# Revit family: Legrand-Enveloppes_industrielles-Metal-Armoires_Altis-P500
name_source: partatom
category: Equipement électrique
units: mm (PartAtom-declared; Revit-internal decimal feet)

## family parameters
Basée sur le plan de construction = Non
Configuration du panneau = Deux colonnes, circuits au sein
Cote de connecteur circulaire = Utiliser le diamètre
Couper avec des vides une fois chargée = Non
Numéro OmniClass = 23.80.30.11.17
Partagée = Non
Point de calcul de pièce = Non
Titre OmniClass = Distribution Boards and Control Panels
Toujours verticalement = Oui
Type d'élément = Tableau de raccordement

## types (15) — shared parameters
Conditions Générale d'Utilisation = https://export.legrand.com
ETIM Class 6.0 = EC000261
Fabricant = Legrand
IK = 10
IP = 55
Matière = Polyester
RAL = 7035
URL = www.legrand.fr
aucun socle = Oui
erreur double hauteur de socle = Non
profondeur = 500 mm  [stored 1.64042 ft]
socle 100mm = Non
socle 200mm = Non
socle hauteur 100 largeur 1000 = Non
socle hauteur 100 largeur 1200 = Non
socle hauteur 100 largeur 1600 = Non
socle hauteur 100 largeur 400 = Non
socle hauteur 100 largeur 600 = Non
socle hauteur 100 largeur 800 = Non
socle hauteur 200 largeur 1000 = Non
socle hauteur 200 largeur 1200 = Non
socle hauteur 200 largeur 1600 = Non
socle hauteur 200 largeur 400 = Non
socle hauteur 200 largeur 600 = Non
socle hauteur 200 largeur 800 = Non
zero-valued in all types: Elévation par défaut, hauteur socles

## per-type parameters (varying)
| type | Armoire 047220 | Armoire 047221 | Armoire 047222 | Armoire 047223 | Armoire 047224 | Armoire 047225 | Armoire 047226 | Armoire 047227 | Armoire 047228 | Armoire 047229 | Armoire 047230 | Armoire 047231 | Armoire 047232 | Armoire 047233 | Armoire 047234 | Description | Hauteur | Image du type | Largeur | Poids | distance avant zone d'installation | largeur zone d'installation | profondeur zone d'installation |
| Enveloppe industrielle - Altis - Assemblable - Métal - Profondeur 500mm - Hauteur 1600mm - Largeur  600mm | Oui | Non | Non | Non | Non | Non | Non | Non | Non | Non | Non | Non | Non | Non | Non | Ref 047220 - Enveloppe industrielle - Altis - Assemblable - Métal - Profondeur 500mm | 1623 mm  [stored 5.3248 ft] | Altis_047101_pw_133028_pz_48.jpg | 600 mm | 70.40 kg | 600 mm | 2200 mm | 1100 mm |
| Enveloppe industrielle - Altis - Assemblable - Métal - Profondeur 500mm - Hauteur 1600mm - Largeur  800mm | Non | Oui | Non | Non | Non | Non | Non | Non | Non | Non | Non | Non | Non | Non | Non | Ref 047221 - Enveloppe industrielle - Altis - Assemblable - Métal - Profondeur 500mm | 1623 mm  [stored 5.3248 ft] | Altis_047101_pw_133028_pz_48.jpg | 800 mm  [stored 2.62467 ft] | 81.00 kg | 800 mm  [stored 2.62467 ft] | 2400 mm | 1300 mm  [stored 4.26509 ft] |
| Enveloppe industrielle - Altis - Assemblable - Métal - Profondeur 500mm - Hauteur 1600mm - Largeur  1200mm | Non | Non | Oui | Non | Non | Non | Non | Non | Non | Non | Non | Non | Non | Non | Non | Ref 047222 - Enveloppe industrielle - Altis - Assemblable - Métal - Profondeur 500mm | 1623 mm  [stored 5.3248 ft] | Altis_047101_pw_133028_pz_48.jpg | 0 mm  [stored 0 ft] | 124.50 kg | 0 mm  [stored 0 ft] | 1600 mm  [stored 5.24934 ft] | 500 mm  [stored 1.64042 ft] |
| Enveloppe industrielle - Altis - Assemblable - Métal - Profondeur 500mm - Hauteur 1800mm - Largeur 400mm | Non | Non | Non | Oui | Non | Non | Non | Non | Non | Non | Non | Non | Non | Non | Non | Ref 047223 - Enveloppe industrielle - Altis - Assemblable - Métal - Profondeur 500mm | 1823 mm  [stored 5.98097 ft] | Altis_047101_pw_133028_pz_48.jpg | 400 mm  [stored 1.31234 ft] | 55.00 kg | 400 mm  [stored 1.31234 ft] | 2000 mm  [stored 6.56168 ft] | 900 mm  [stored 2.95276 ft] |
| Enveloppe industrielle - Altis - Assemblable - Métal - Profondeur 500mm - Hauteur 1800mm - Largeur 600mm | Non | Non | Non | Non | Oui | Non | Non | Non | Non | Non | Non | Non | Non | Non | Non | Ref 047224 - Enveloppe industrielle - Altis - Assemblable - Métal - Profondeur 500mm | 1823 mm  [stored 5.98097 ft] | Altis_047101_pw_133028_pz_48.jpg | 600 mm | 74.30 kg | 600 mm | 2200 mm | 1100 mm |
| Enveloppe industrielle - Altis - Assemblable - Métal - Profondeur 500mm - Hauteur 1800mm - Largeur 800mm | Non | Non | Non | Non | Non | Oui | Non | Non | Non | Non | Non | Non | Non | Non | Non | Ref 047225 - Enveloppe industrielle - Altis - Assemblable - Métal - Profondeur 500mm | 1823 mm  [stored 5.98097 ft] | Altis_047101_pw_133028_pz_48.jpg | 800 mm  [stored 2.62467 ft] | 86.00 kg | 800 mm  [stored 2.62467 ft] | 2400 mm | 1300 mm  [stored 4.26509 ft] |
| Enveloppe industrielle - Altis - Assemblable - Métal - Profondeur 500mm - Hauteur 1800mm - Largeur 1000mm - Avec recentrage porte | Non | Non | Non | Non | Non | Non | Oui | Non | Non | Non | Non | Non | Non | Non | Non | Ref 047226 - Enveloppe industrielle - Altis - Assemblable - Métal - Profondeur 500mm | 1823 mm  [stored 5.98097 ft] | <Aucun> | 1000 mm  [stored 3.28084 ft] | 99.30 kg | 1000 mm  [stored 3.28084 ft] | 2600 mm  [stored 8.53018 ft] | 1500 mm  [stored 4.92126 ft] |
| Enveloppe industrielle - Altis - Assemblable - Métal - Profondeur 500mm - Hauteur 1800mm - Largeur 1200mm | Non | Non | Non | Non | Non | Non | Non | Oui | Non | Non | Non | Non | Non | Non | Non | Ref 047227 - Enveloppe industrielle - Altis - Assemblable - Métal - Profondeur 500mm | 1823 mm  [stored 5.98097 ft] | Altis_047101_pw_133028_pz_48.jpg | 1200 mm | 131.40 kg | 1200 mm | 2800 mm  [stored 9.18635 ft] | 1700 mm  [stored 5.57743 ft] |
| Enveloppe industrielle - Altis - Assemblable - Métal - Profondeur 500mm - Hauteur 2000mm - Largeur  400mm | Non | Non | Non | Non | Non | Non | Non | Non | Oui | Non | Non | Non | Non | Non | Non | Ref 047228 - Enveloppe industrielle - Altis - Assemblable - Métal - Profondeur 500mm | 2023 mm  [stored 6.63714 ft] | Altis_047101_pw_133028_pz_48.jpg | 400 mm  [stored 1.31234 ft] | 57.50 kg | 400 mm  [stored 1.31234 ft] | 2000 mm  [stored 6.56168 ft] | 900 mm  [stored 2.95276 ft] |
| Enveloppe industrielle - Altis - Assemblable - Métal - Profondeur 500mm - Hauteur 2000mm - Largeur  600mm | Non | Non | Non | Non | Non | Non | Non | Non | Non | Oui | Non | Non | Non | Non | Non | Ref 047229 - Enveloppe industrielle - Altis - Assemblable - Métal - Profondeur 500mm | 2023 mm  [stored 6.63714 ft] | Altis_047101_pw_133028_pz_48.jpg | 600 mm | 79.20 kg | 600 mm | 2200 mm | 1100 mm |
| Enveloppe industrielle - Altis - Assemblable - Métal - Profondeur 500mm - Hauteur 2000mm - Largeur  800mm | Non | Non | Non | Non | Non | Non | Non | Non | Non | Non | Oui | Non | Non | Non | Non | Ref 047230 - Enveloppe industrielle - Altis - Assemblable - Métal - Profondeur 500mm | 2023 mm  [stored 6.63714 ft] | Altis_047101_pw_133028_pz_48.jpg | 800 mm  [stored 2.62467 ft] | 92.70 kg | 800 mm  [stored 2.62467 ft] | 2400 mm | 1300 mm  [stored 4.26509 ft] |
| Enveloppe industrielle - Altis - Assemblable - Métal - Profondeur 500mm - Hauteur 2000mm - Largeur 1000mm - Avec recentrage porte | Non | Non | Non | Non | Non | Non | Non | Non | Non | Non | Non | Oui | Non | Non | Non | Ref 047231 - Enveloppe industrielle - Altis - Assemblable - Métal - Profondeur 500mm | 2023 mm  [stored 6.63714 ft] | <Aucun> | 1000 mm  [stored 3.28084 ft] | 106.00 kg | 1000 mm  [stored 3.28084 ft] | 2600 mm  [stored 8.53018 ft] | 1500 mm  [stored 4.92126 ft] |
| Enveloppe industrielle - Altis - Assemblable - Métal - Profondeur 500mm - Hauteur 2000mm - Largeur  1000mm | Non | Non | Non | Non | Non | Non | Non | Non | Non | Non | Non | Non | Oui | Non | Non | Ref 047232 - Enveloppe industrielle - Altis - Assemblable - Métal - Profondeur 500mm | 2023 mm  [stored 6.63714 ft] | Altis_047101_pw_133028_pz_48.jpg | 1000 mm  [stored 3.28084 ft] | 110.70 kg | 1000 mm  [stored 3.28084 ft] | 2600 mm  [stored 8.53018 ft] | 1500 mm  [stored 4.92126 ft] |
| Enveloppe industrielle - Altis - Assemblable - Métal - Profondeur 500mm - Hauteur 2000mm - Largeur 1200mm | Non | Non | Non | Non | Non | Non | Non | Non | Non | Non | Non | Non | Non | Oui | Non | Ref 047233 - Enveloppe industrielle - Altis - Assemblable - Métal - Profondeur 500mm | 2023 mm  [stored 6.63714 ft] | Altis_047101_pw_133028_pz_48.jpg | 1200 mm | 138.00 kg | 1200 mm | 2800 mm  [stored 9.18635 ft] | 1700 mm  [stored 5.57743 ft] |
| Enveloppe industrielle - Altis - Assemblable - Métal - Profondeur 500mm - Hauteur 2000mm - Largeur 1600mm | Non | Non | Non | Non | Non | Non | Non | Non | Non | Non | Non | Non | Non | Non | Oui | Ref 047234 - Enveloppe industrielle - Altis - Assemblable - Métal - Profondeur 500mm | 2023 mm  [stored 6.63714 ft] | Altis_047101_pw_133028_pz_48.jpg | 1600 mm  [stored 5.24934 ft] | 147.00 kg | 1600 mm  [stored 5.24934 ft] | 3200 mm  [stored 10.4987 ft] | 2100 mm |

note: [stored X ft] marks values corroborated as IEEE doubles in the binary element streams (Revit-internal decimal feet)
